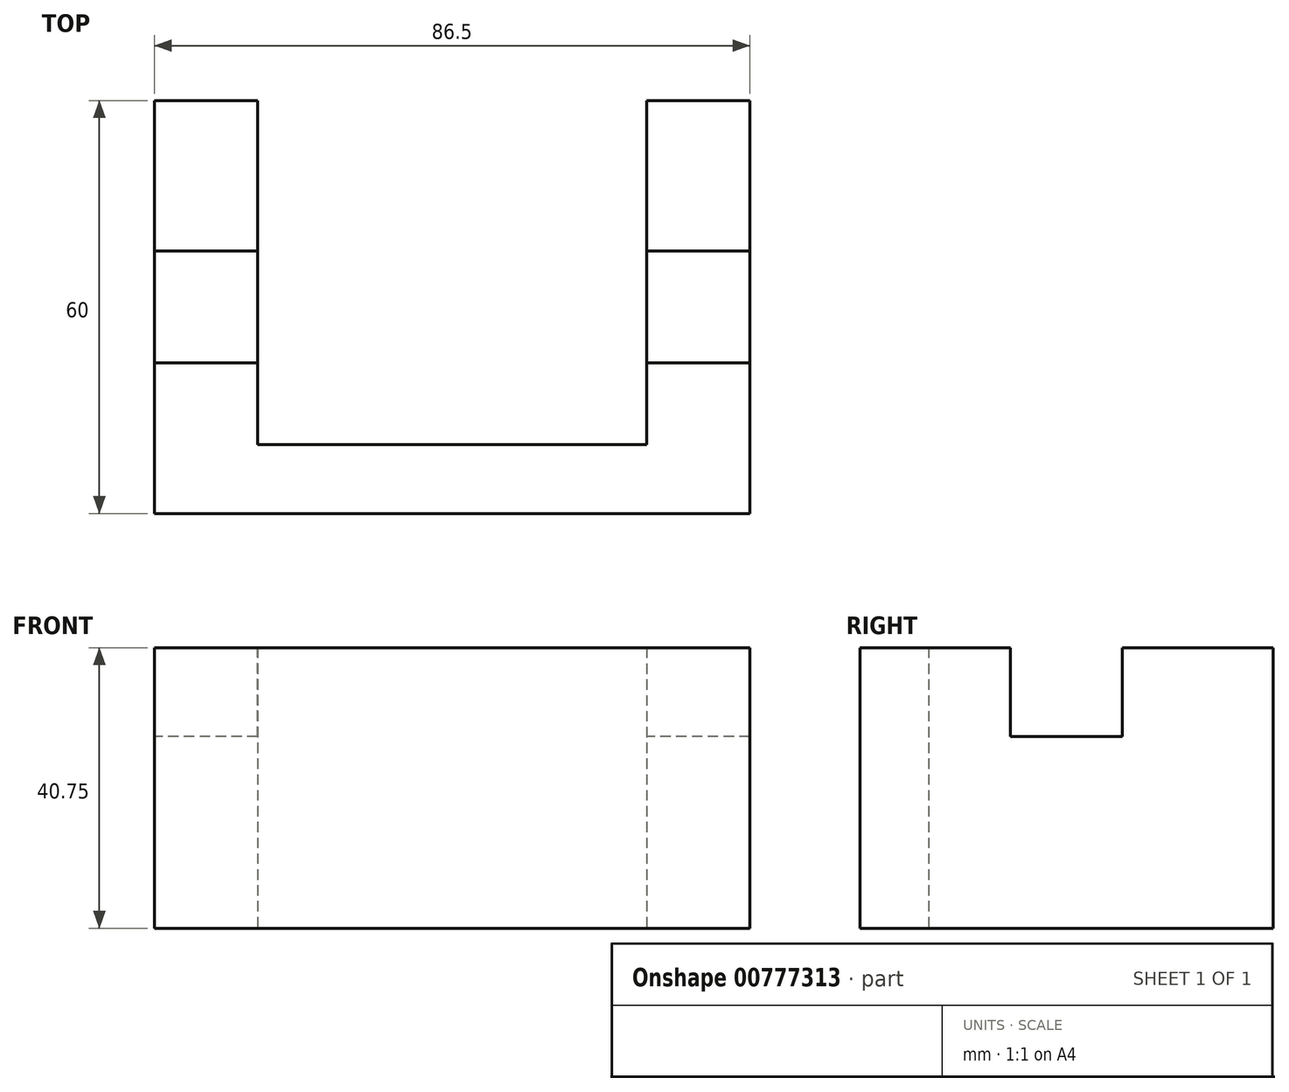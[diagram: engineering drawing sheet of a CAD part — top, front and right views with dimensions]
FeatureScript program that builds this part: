
annotation { "Feature Type Name" : "Feature", "Feature Type Description" : "" }
export const myFeature = defineFeature(function(context is Context, id is Id, definition is map)
    precondition{}
    {
        {
            var Q0;
            Q0=qCreatedBy(makeId("Top.planeOp"),FACE);
            var sketch = newSketch(context, id + "F0", { "sketchPlane" : qUnion([Q0])});
            skLineSegment(sketch, "E0.bottom", {"start": v(7.5, 30) * mm, "end": v(-7.5, 30) * mm});
            skLineSegment(sketch, "E0.top", {"start": v(7.5, -30) * mm, "end": v(-7.5, -30) * mm});
            skLineSegment(sketch, "E0.left", {"start": v(7.5, 30) * mm, "end": v(7.5, -30) * mm});
            skLineSegment(sketch, "E0.right", {"start": v(-7.5, 30) * mm, "end": v(-7.5, -30) * mm});
            skPoint(sketch, "E0.middle", {"position": v(0, 0) * mm});
            skSolve(sketch);
        }
        {
            var Q0;
            Q0=qSketchRegion(id+"F0",true);
            extrude(context, id + "F1", {"entities" : qUnion([Q0]), "depth" : 28.5 * mm, "offsetDistance" : 25 * mm});
        }
        {
            var Q0;
            Q0=makeQuery(id+"F1.opExtrude","CAP_FACE",FACE,{"disambiguationData":[OSD([sQuery(id+"F0.wireOp",EDGE,"E0.bottom"),sQuery(id+"F0.wireOp",EDGE,"E0.top"),sQuery(id+"F0.wireOp",EDGE,"E0.left"),sQuery(id+"F0.wireOp",EDGE,"E0.right")])],"isStart":false});
            var sketch = newSketch(context, id + "F2", { "sketchPlane" : qUnion([Q0])});
            skLineSegment(sketch, "E1.bottom", {"start": v(7.5, 8.12) * mm, "end": v(-7.5, 8.12) * mm});
            skLineSegment(sketch, "E1.top", {"start": v(7.5, -8.12) * mm, "end": v(-7.5, -8.12) * mm});
            skLineSegment(sketch, "E1.left", {"start": v(7.5, 8.12) * mm, "end": v(7.5, -8.12) * mm});
            skLineSegment(sketch, "E1.right", {"start": v(-7.5, 8.12) * mm, "end": v(-7.5, -8.12) * mm});
            skPoint(sketch, "E1.middle", {"position": v(0, 0) * mm});
            skSolve(sketch);
        }
        {
            var Q0;
            {var subQ0=sQuery(id+"F0.wireOp",EDGE,"E0.left");Q0=makeQuery(id+"F411Q4QD505CHMR_1.boolean.opBoolean","MERGE",FACE,{"derivedFrom":[makeQuery(id+"F1.opExtrude","CAP_FACE",FACE,{"disambiguationData":[OSD([sQuery(id+"F0.wireOp",EDGE,"E0.bottom"),sQuery(id+"F0.wireOp",EDGE,"E0.top"),subQ0,sQuery(id+"F0.wireOp",EDGE,"E0.right")])],"isStart":true}),makeQuery(id+"F411Q4QD505CHMR_1.opExtrude","SWEPT_FACE",FACE,{"disambiguationData":[OSD([subQ0]),TDD([makeQuery(id+"F1.opExtrude","CAP_EDGE",EDGE,{"disambiguationData":[OSD([subQ0])],"isStart":true})])]})]});}
            var sketch = newSketch(context, id + "F3", { "sketchPlane" : qUnion([Q0])});
            skLineSegment(sketch, "E2.bottom", {"start": v(7.5, 20) * mm, "end": v(64, 20) * mm});
            skLineSegment(sketch, "E2.top", {"start": v(7.5, -30) * mm, "end": v(64, -30) * mm});
            skLineSegment(sketch, "E2.left", {"start": v(7.5, 20) * mm, "end": v(7.5, -30) * mm});
            skLineSegment(sketch, "E2.right", {"start": v(64, 20) * mm, "end": v(64, -30) * mm});
            skSolve(sketch);
        }
        {
            var Q0;
            Q0=makeQuery(id+"F3.imprint","IMPRINT",FACE,{"disambiguationData":[TD([[makeQuery(id+"F3.imprint","IMPRINT",EDGE,{"derivedFrom":sQuery(id+"F3.wireOp",EDGE,"E2.bottom")}),-1.0]])]});
            extrude(context, id + "F4", {"entities" : qUnion([Q0]), "operationType" : NewBodyOperationType.REMOVE, "endBound" : BoundingType.THROUGH_ALL, "oppositeDirection" : true, "depth" : 25 * mm, "offsetDistance" : 25 * mm});
        }
        {
            var Q0;
            {var subQ0=sQuery(id+"F2.wireOp",EDGE,"E1.bottom");Q0=makeQuery(id+"F2.imprint","IMPRINT",FACE,{"disambiguationData":[TD([[makeQuery(id+"F2.imprint","IMPRINT",EDGE,{"derivedFrom":subQ0}),-1.0]])]});}
            var Q1;
            {var subQ0=sQuery(id+"F2.wireOp",EDGE,"E1.top");Q1=makeQuery(id+"F2.imprint","IMPRINT",FACE,{"disambiguationData":[TD([[makeQuery(id+"F2.imprint","IMPRINT",EDGE,{"derivedFrom":subQ0}),1.0]])]});}
            extrude(context, id + "F5", {"entities" : qUnion([Q0, Q1]), "operationType" : NewBodyOperationType.ADD, "depth" : 12.25 * mm, "offsetDistance" : 25 * mm});
        }
        {
            var Q0;
            {var subQ0=sQuery(id+"F0.wireOp",EDGE,"E0.left");var subQ1=makeQuery(id+"F1.opExtrude","CAP_EDGE",EDGE,{"disambiguationData":[OSD([subQ0])],"isStart":false});Q0=makeQuery(id+"F5.boolean.opBoolean","MERGE",FACE,{"derivedFrom":[makeQuery(id+"F1.opExtrude","SWEPT_FACE",FACE,{"disambiguationData":[OSD([subQ0])]}),makeQuery(id+"F5.opExtrude","SWEPT_FACE",FACE,{"disambiguationData":[OSD([subQ0]),TDD([makeQuery(id+"F2.imprint","IMPRINT",EDGE,{"disambiguationData":[TD([[makeQuery(id+"F2.imprint","INTERSECT",VERTEX,{"derivedFrom":[makeQuery(id+"F1.opExtrude","CAP_EDGE",EDGE,{"disambiguationData":[OSD([sQuery(id+"F0.wireOp",EDGE,"E0.bottom")])],"isStart":false}),subQ1]}),-1.0]])],"derivedFrom":subQ1})])]}),makeQuery(id+"F5.opExtrude","SWEPT_FACE",FACE,{"disambiguationData":[OSD([subQ0]),TDD([makeQuery(id+"F2.imprint","IMPRINT",EDGE,{"disambiguationData":[TD([[makeQuery(id+"F2.imprint","INTERSECT",VERTEX,{"derivedFrom":[makeQuery(id+"F1.opExtrude","CAP_EDGE",EDGE,{"disambiguationData":[OSD([sQuery(id+"F0.wireOp",EDGE,"E0.top")])],"isStart":false}),subQ1]}),1.0]])],"derivedFrom":subQ1})])]})]});}
            extrude(context, id + "F6", {"entities" : qUnion([Q0]), "operationType" : NewBodyOperationType.ADD, "depth" : 71.5 * mm, "offsetDistance" : 25 * mm});
        }
        {
            var Q0;
            Q0=qSketchRegion(id+"F3",true);
            extrude(context, id + "F7", {"entities" : qUnion([Q0]), "operationType" : NewBodyOperationType.REMOVE, "endBound" : BoundingType.THROUGH_ALL, "oppositeDirection" : true, "depth" : 25 * mm, "offsetDistance" : 25 * mm});
        }
        {
            var Q0;
            {var subQ1=sQuery(id+"F0.wireOp",EDGE,"E0.right");var subQ3=sQuery(id+"F0.wireOp",EDGE,"E0.bottom");var subQ7=sQuery(id+"F0.wireOp",EDGE,"E0.left");var subQ8=sQuery(id+"F0.wireOp",EDGE,"E0.top");Q0=makeQuery(id+"F7.boolean.opBoolean","SPLIT",FACE,{"disambiguationData":[TD([makeQuery(id+"F1.opExtrude","SWEPT_FACE",FACE,{"disambiguationData":[OSD([subQ1])]})])],"derivedFrom":makeQuery(id+"F6.boolean.opBoolean","MERGE",FACE,{"derivedFrom":[makeQuery(id+"F1.opExtrude","CAP_FACE",FACE,{"disambiguationData":[OSD([subQ3,subQ8,subQ7,subQ1])],"isStart":false}),makeQuery(id+"F6.opExtrude","SWEPT_FACE",FACE,{"disambiguationData":[OSD([subQ7]),TDD([makeQuery(id+"F1.opExtrude","CAP_EDGE",EDGE,{"disambiguationData":[OSD([subQ7])],"isStart":false})])]})]})});}
            var Q1;
            {var subQ2=sQuery(id+"F0.wireOp",EDGE,"E0.left");Q1=makeQuery(id+"F7.boolean.opBoolean","SPLIT",FACE,{"disambiguationData":[TD([makeQuery(id+"F6.opExtrude","CAP_FACE",FACE,{"disambiguationData":[OSD([subQ2])],"isStart":false})])],"derivedFrom":makeQuery(id+"F6.boolean.opBoolean","MERGE",FACE,{"derivedFrom":[makeQuery(id+"F1.opExtrude","CAP_FACE",FACE,{"disambiguationData":[OSD([sQuery(id+"F0.wireOp",EDGE,"E0.bottom"),sQuery(id+"F0.wireOp",EDGE,"E0.top"),subQ2,sQuery(id+"F0.wireOp",EDGE,"E0.right")])],"isStart":false}),makeQuery(id+"F6.opExtrude","SWEPT_FACE",FACE,{"disambiguationData":[OSD([subQ2]),TDD([makeQuery(id+"F1.opExtrude","CAP_EDGE",EDGE,{"disambiguationData":[OSD([subQ2])],"isStart":false})])]})]})});}
            extrude(context, id + "F8", {"entities" : qUnion([Q0, Q1]), "operationType" : NewBodyOperationType.REMOVE, "oppositeDirection" : true, "depth" : .66 * mm, "offsetDistance" : 25 * mm});
        }
    });
